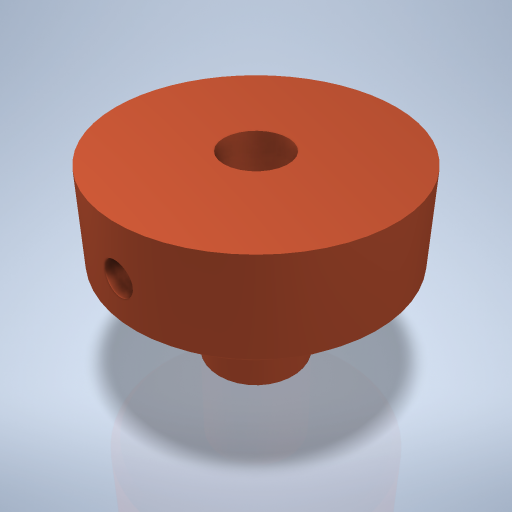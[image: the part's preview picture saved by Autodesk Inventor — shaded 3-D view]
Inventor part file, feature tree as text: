
AUTODESK INVENTOR PART (.ipt)
format: ipt  version: 2024.2 (Build 282272000, 272)  size: 269,824 bytes
history: native  units: mm
features: sketch x3, hole x2, revolve x1, mirror x1, chamfer x1
ambient origin geometry x8: Origin, YZ Plane, XZ Plane, XY Plane, X Axis, Y Axis, Z Axis, Center Point
bodies: Volumenkörper1 (feature_tree)
feature tree (8):
  revolve  "Umdrehung1"
  hole  "Bohrung1"  [1 undecoded]
  hole  "Bohrung2"  [1 undecoded]
  mirror  "Spiegeln1"
  chamfer  "Fasen1"  Distance=5.0mm
  sketch  "Skizze1"  dims[d0=10.0mm d1=10.0mm]
  sketch  "Skizze2"  dims[d2=10.0mm d3=28.0mm]
  sketch  "Skizze4"  dims[d4=90.0deg d5=6.5mm d6=6.0mm d7=4.0mm d8=2.0mm d9=90.0deg d10=1.0mm d11=0.0mm d12=5.0mm d13=3.242mm d14=8.0mm d15=4.0mm d16=2.0mm d17=90.0deg d18=8.0mm d19=0.0mm d20=1.0mm d21=2.0mm d22=45.0deg]
note: 2 required parameter values undecoded (feature->parameter linkage not recoverable at this tier; creation-order binding heuristic only, values carry confidence <= 0.55)
